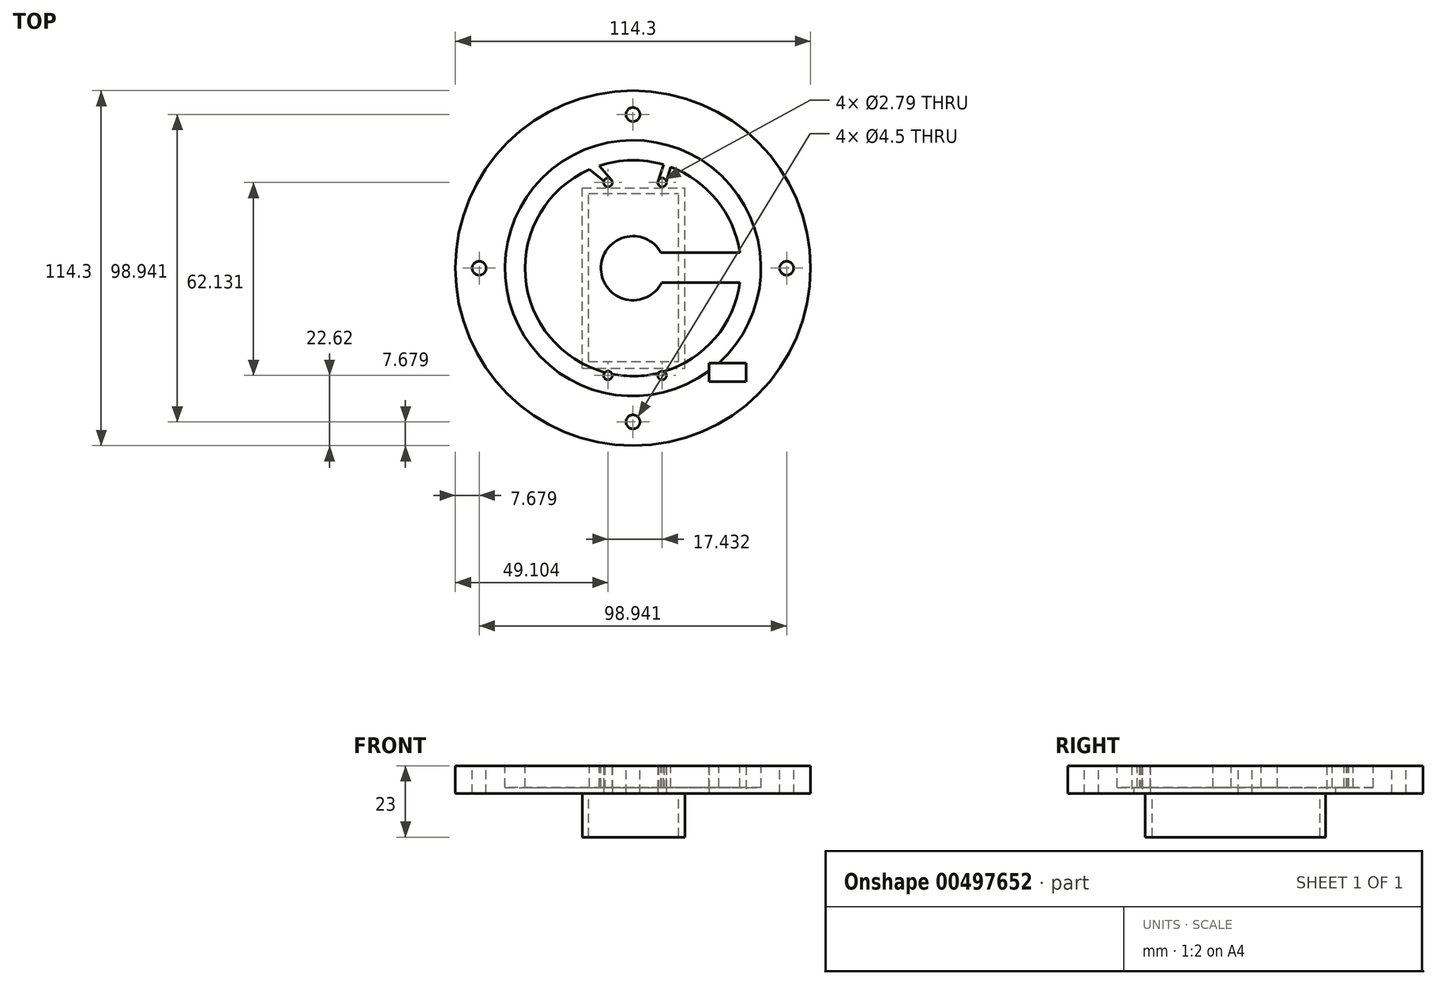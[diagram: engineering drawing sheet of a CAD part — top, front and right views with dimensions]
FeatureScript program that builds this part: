
annotation { "Feature Type Name" : "Feature", "Feature Type Description" : "" }
export const myFeature = defineFeature(function(context is Context, id is Id, definition is map)
    precondition{}
    {
        {
            var Q0;
            Q0=qCreatedBy(makeId("Top.planeOp"),FACE);
            var sketch = newSketch(context, id + "F0", { "sketchPlane" : qUnion([Q0])});
            skCircle(sketch, "E0", {"center": v(0, 0) * mm, "radius": 57.15 * mm});
            skLineSegment(sketch, "E1", {"start": v(0, 0) * mm, "end": v(-90.89, 0) * mm, "construction": true});
            skLineSegment(sketch, "E2", {"start": v(0, 0) * mm, "end": v(91.48, 0) * mm, "construction": true});
            skSolve(sketch);
        }
        {
            var Q0;
            Q0=makeQuery(id+"F0.imprint","IMPRINT",FACE,{"disambiguationData":[TD([[makeQuery(id+"F0.imprint","IMPRINT",EDGE,{"derivedFrom":sQuery(id+"F0.wireOp",EDGE,"E0")}),1.0]])]});
            extrude(context, id + "F1", {"entities" : qUnion([Q0]), "depth" : 9 * mm});
        }
        {
            var Q0;
            Q0=makeQuery(id+"F1.opExtrude","CAP_FACE",FACE,{"disambiguationData":[OSD([sQuery(id+"F0.wireOp",EDGE,"E0")])],"isStart":false});
            var sketch = newSketch(context, id + "F2", { "sketchPlane" : qUnion([Q0])});
            skCircle(sketch, "E3", {"center": v(0, 0) * mm, "radius": 41.18 * mm});
            skCircle(sketch, "E4", {"center": v(0, 0) * mm, "radius": 34.74 * mm});
            skSolve(sketch);
        }
        {
            var Q0;
            Q0=makeQuery(id+"F2.imprint","IMPRINT",FACE,{"disambiguationData":[TD([[makeQuery(id+"F2.imprint","IMPRINT",EDGE,{"derivedFrom":sQuery(id+"F2.wireOp",EDGE,"E3")}),1.0]])]});
            extrude(context, id + "F3", {"entities" : qUnion([Q0]), "operationType" : NewBodyOperationType.REMOVE, "oppositeDirection" : true, "depth" : 7 * mm});
        }
        {
            var Q0;
            Q0=makeQuery(id+"F3.boolean.opBoolean","SPLIT",FACE,{"disambiguationData":[TD([makeQuery(id+"F3.opExtrude","SWEPT_FACE",FACE,{"disambiguationData":[OSD([sQuery(id+"F2.wireOp",EDGE,"E4")])]})])],"derivedFrom":makeQuery(id+"F1.opExtrude","CAP_FACE",FACE,{"disambiguationData":[OSD([sQuery(id+"F0.wireOp",EDGE,"E0")])],"isStart":false})});
            var sketch = newSketch(context, id + "F4", { "sketchPlane" : qUnion([Q0])});
            skCircle(sketch, "E5", {"center": v(0, 0) * mm, "radius": 10.31 * mm});
            skLineSegment(sketch, "E6.bottom", {"start": v(8.97, 5.07) * mm, "end": v(37.77, 5.07) * mm});
            skLineSegment(sketch, "E6.top", {"start": v(8.97, -4.58) * mm, "end": v(37.77, -4.58) * mm});
            skLineSegment(sketch, "E6.left", {"start": v(8.97, 5.07) * mm, "end": v(8.97, -4.58) * mm});
            skLineSegment(sketch, "E6.right", {"start": v(37.77, 5.07) * mm, "end": v(37.77, -4.58) * mm});
            skSolve(sketch);
        }
        {
            var Q0;
            {var subQ0=sQuery(id+"F4.wireOp",EDGE,"E6.left");Q0=makeQuery(id+"F4.imprint","IMPRINT",FACE,{"disambiguationData":[TD([[makeQuery(id+"F4.imprint","IMPRINT",EDGE,{"derivedFrom":subQ0}),1.0]])]});}
            var Q1;
            {var subQ0=sQuery(id+"F4.wireOp",EDGE,"E6.right");Q1=makeQuery(id+"F4.imprint","IMPRINT",FACE,{"disambiguationData":[TD([[makeQuery(id+"F4.imprint","IMPRINT",EDGE,{"derivedFrom":subQ0}),-1.0]])]});}
            var Q2;
            {var subQ0=sQuery(id+"F4.wireOp",EDGE,"E6.left");Q2=makeQuery(id+"F4.imprint","IMPRINT",FACE,{"disambiguationData":[TD([[makeQuery(id+"F4.imprint","IMPRINT",EDGE,{"derivedFrom":subQ0}),-1.0]])]});}
            var Q3;
            {var subQ1=sQuery(id+"F4.wireOp",EDGE,"E5");var subQ3=sQuery(id+"F4.wireOp",EDGE,"E6.top");var subQ4=makeQuery(id+"F4.imprint","INTERSECT",VERTEX,{"derivedFrom":[subQ1,subQ3]});Q3=makeQuery(id+"F4.imprint","IMPRINT",FACE,{"disambiguationData":[TD([[makeQuery(id+"F4.imprint","IMPRINT",EDGE,{"disambiguationData":[TD([[subQ4,-1.0]])],"derivedFrom":subQ3}),1.0]])]});}
            extrude(context, id + "F5", {"entities" : qUnion([Q0, Q1, Q2, Q3]), "operationType" : NewBodyOperationType.REMOVE, "oppositeDirection" : true, "depth" : 7 * mm});
        }
        {
            var Q0;
            Q0=makeQuery(id+"F1.opExtrude","CAP_FACE",FACE,{"disambiguationData":[OSD([sQuery(id+"F0.wireOp",EDGE,"E0")])],"isStart":true});
            var sketch = newSketch(context, id + "F6", { "sketchPlane" : qUnion([Q0])});
            skLineSegment(sketch, "E7.bottom", {"start": v(24.43, 36.54) * mm, "end": v(36.43, 36.54) * mm});
            skLineSegment(sketch, "E7.top", {"start": v(24.43, 30.54) * mm, "end": v(36.43, 30.54) * mm});
            skLineSegment(sketch, "E7.left", {"start": v(24.43, 36.54) * mm, "end": v(24.43, 30.54) * mm});
            skLineSegment(sketch, "E7.right", {"start": v(36.43, 36.54) * mm, "end": v(36.43, 30.54) * mm});
            skSolve(sketch);
        }
        {
            var Q0;
            Q0=qSketchRegion(id+"F6",true);
            extrude(context, id + "F7", {"entities" : qUnion([Q0]), "operationType" : NewBodyOperationType.REMOVE, "oppositeDirection" : true, "depth" : 9 * mm});
        }
        {
            var Q0;
            {var subQ0=sQuery(id+"F0.wireOp",EDGE,"E0");Q0=makeQuery(id+"F3.boolean.opBoolean","SPLIT",FACE,{"disambiguationData":[TD([makeQuery(id+"F1.opExtrude","SWEPT_FACE",FACE,{"disambiguationData":[OSD([subQ0])]})])],"derivedFrom":makeQuery(id+"F1.opExtrude","CAP_FACE",FACE,{"disambiguationData":[OSD([subQ0])],"isStart":false})});}
            var sketch = newSketch(context, id + "F8", { "sketchPlane" : qUnion([Q0])});
            skCircle(sketch, "E8", {"center": v(0, 0) * mm, "radius": 49.47 * mm});
            skPoint(sketch, "E9", {"position": v(0, 49.47) * mm});
            skPoint(sketch, "E10", {"position": v(0, -49.47) * mm});
            skPoint(sketch, "E11", {"position": v(49.47, 0) * mm});
            skPoint(sketch, "E12", {"position": v(-49.47, 0) * mm});
            skSolve(sketch);
        }
        {
            var Q0;
            Q0=sQuery(id+"F8.wireOp",VERTEX,"E9");
            var Q1;
            Q1=sQuery(id+"F8.wireOp",VERTEX,"E12");
            var Q2;
            Q2=sQuery(id+"F8.wireOp",VERTEX,"E10");
            var Q3;
            Q3=sQuery(id+"F8.wireOp",VERTEX,"E11");
            var Q4;
            Q4=makeQuery(id+"F1.opExtrude","SWEPT_BODY",BODY,{"disambiguationData":[OSD([sQuery(id+"F0.wireOp",EDGE,"E0")])]});
            hole(context, id + "F9", {"style" : HoleStyle.SIMPLE, "endStyle" : HoleEndStyle.THROUGH, "standardTappedOrClearance" : lookupTablePath({ "standard" : "ANSI", "fit" : "Normal (ASME)", "size" : "#8", "type" : "Clearance" }), "standardBlindInLast" : lookupTablePath({ "fit" : "Free", "standard" : "ANSI", "size" : "#8", "type" : "Clearance" }), "holeDiameter" : 4.5 * mm, "isTappedThrough" : true, "tappedDepth" : 12.7 * mm, "tapClearance" : 3, "locations" : qUnion([Q0, Q1, Q2, Q3]), "scope" : qUnion([Q4])});
        }
        {
            var Q0;
            Q0=makeQuery(id+"F1.opExtrude","CAP_FACE",FACE,{"disambiguationData":[OSD([sQuery(id+"F0.wireOp",EDGE,"E0")])],"isStart":true});
            var sketch = newSketch(context, id + "F10", { "sketchPlane" : qUnion([Q0])});
            skLineSegment(sketch, "E13.bottom", {"start": v(-14.3, 29.98) * mm, "end": v(14.7, 29.98) * mm});
            skLineSegment(sketch, "E13.top", {"start": v(-14.3, -24.02) * mm, "end": v(14.7, -24.02) * mm});
            skLineSegment(sketch, "E13.left", {"start": v(-14.3, 29.98) * mm, "end": v(-14.3, -24.02) * mm});
            skLineSegment(sketch, "E13.right", {"start": v(14.7, 29.98) * mm, "end": v(14.7, -24.02) * mm});
            skLineSegment(sketch, "E14.bottom", {"start": v(-16.31, 32.19) * mm, "end": v(16.69, 32.19) * mm});
            skLineSegment(sketch, "E14.top", {"start": v(-16.31, -25.81) * mm, "end": v(16.69, -25.81) * mm});
            skLineSegment(sketch, "E14.left", {"start": v(-16.31, 32.19) * mm, "end": v(-16.31, -25.81) * mm});
            skLineSegment(sketch, "E14.right", {"start": v(16.69, 32.19) * mm, "end": v(16.69, -25.81) * mm});
            skSolve(sketch);
        }
        {
            var Q0;
            Q0=makeQuery(id+"F10.imprint","IMPRINT",FACE,{"disambiguationData":[TD([[makeQuery(id+"F10.imprint","IMPRINT",EDGE,{"derivedFrom":sQuery(id+"F10.wireOp",EDGE,"E13.bottom")}),1.0]])]});
            extrude(context, id + "F11", {"entities" : qUnion([Q0]), "operationType" : NewBodyOperationType.ADD, "depth" : 14 * mm});
        }
        {
            var Q0;
            {var subQ0=sQuery(id+"F0.wireOp",EDGE,"E0");Q0=makeQuery(id+"F11.boolean.opBoolean","SPLIT",FACE,{"disambiguationData":[TD([makeQuery(id+"F1.opExtrude","SWEPT_FACE",FACE,{"disambiguationData":[OSD([subQ0])]})])],"derivedFrom":makeQuery(id+"F1.opExtrude","CAP_FACE",FACE,{"disambiguationData":[OSD([subQ0])],"isStart":true})});}
            var sketch = newSketch(context, id + "F12", { "sketchPlane" : qUnion([Q0])});
            skPoint(sketch, "E15", {"position": v(-8.05, 34.53) * mm});
            skPoint(sketch, "E16", {"position": v(9.39, 34.53) * mm});
            skPoint(sketch, "E17", {"position": v(-8.05, -27.6) * mm});
            skPoint(sketch, "E18", {"position": v(9.39, -27.6) * mm});
            skSolve(sketch);
        }
        {
            var Q0;
            Q0=sQuery(id+"F12.wireOp",VERTEX,"E15");
            var Q1;
            Q1=sQuery(id+"F12.wireOp",VERTEX,"E16");
            var Q2;
            Q2=sQuery(id+"F12.wireOp",VERTEX,"E17");
            var Q3;
            Q3=sQuery(id+"F12.wireOp",VERTEX,"E18");
            var Q4;
            Q4=makeQuery(id+"F1.opExtrude","SWEPT_BODY",BODY,{"disambiguationData":[OSD([sQuery(id+"F0.wireOp",EDGE,"E0")])]});
            hole(context, id + "F13", {"style" : HoleStyle.SIMPLE, "endStyle" : HoleEndStyle.THROUGH, "standardTappedOrClearance" : lookupTablePath({ "standard" : "ANSI", "fit" : "Normal (ASME)", "size" : "#3", "type" : "Clearance" }), "standardBlindInLast" : lookupTablePath({ "fit" : "Free", "standard" : "ANSI", "size" : "#3", "type" : "Clearance" }), "holeDiameter" : 2.8 * mm, "isTappedThrough" : true, "tappedDepth" : 12.7 * mm, "tapClearance" : 3, "locations" : qUnion([Q0, Q1, Q2, Q3]), "scope" : qUnion([Q4])});
        }
        {
            var Q0;
            Q0=makeQuery(id+"F3.boolean.opBoolean","SPLIT",FACE,{"disambiguationData":[TD([makeQuery(id+"F3.opExtrude","SWEPT_FACE",FACE,{"disambiguationData":[OSD([sQuery(id+"F2.wireOp",EDGE,"E4")])]})])],"derivedFrom":makeQuery(id+"F1.opExtrude","CAP_FACE",FACE,{"disambiguationData":[OSD([sQuery(id+"F0.wireOp",EDGE,"E0")])],"isStart":false})});
            var sketch = newSketch(context, id + "F14", { "sketchPlane" : qUnion([Q0])});
            skLineSegment(sketch, "E19", {"start": v(-9.37, 28.04) * mm, "end": v(-14.06, 31.76) * mm});
            skLineSegment(sketch, "E20", {"start": v(-11.71, 34.07) * mm, "end": v(-6.98, 28.5) * mm});
            skPoint(sketch, "E20.startSnap0", {"position": v(-11.71, 29.9) * mm});
            skLineSegment(sketch, "E21", {"start": v(8.06, 28.04) * mm, "end": v(10.23, 34.63) * mm});
            skLineSegment(sketch, "E22", {"start": v(10.71, 28.04) * mm, "end": v(12.53, 33.75) * mm});
            skSolve(sketch);
        }
        {
            var Q0;
            {var subQ0=sQuery(id+"F14.wireOp",EDGE,"E19");Q0=makeQuery(id+"F14.imprint","IMPRINT",FACE,{"disambiguationData":[TD([[makeQuery(id+"F14.imprint","IMPRINT",EDGE,{"derivedFrom":subQ0}),-1.0]])]});}
            var Q1;
            {var subQ0=sQuery(id+"F14.wireOp",EDGE,"E21");var subQ1=sQuery(id+"F2.wireOp",EDGE,"E4");var subQ2=makeQuery(id+"F3.opExtrude","SWEPT_FACE",FACE,{"disambiguationData":[OSD([subQ1])]});var subQ3=makeQuery(id+"F1.opExtrude","CAP_FACE",FACE,{"disambiguationData":[OSD([sQuery(id+"F0.wireOp",EDGE,"E0")])],"isStart":false});var subQ4=makeQuery(id+"F13.hole-3.boolean.opBoolean","INTERSECT",EDGE,{"derivedFrom":[makeQuery(id+"F3.boolean.opBoolean","SPLIT",FACE,{"disambiguationData":[TD([subQ2])],"derivedFrom":subQ3}),makeQuery(id+"F13.hole-3.opRevolve","SWEPT_FACE",FACE,{"disambiguationData":[OSD([sQuery(id+"F13.hole-3.sketch.wireOp",EDGE,"core_line_2")])]})]});var subQ5=makeQuery(id+"F14.imprint","INTERSECT",VERTEX,{"derivedFrom":[subQ4,subQ0]});Q1=makeQuery(id+"F14.imprint","IMPRINT",FACE,{"disambiguationData":[TD([[makeQuery(id+"F14.imprint","IMPRINT",EDGE,{"disambiguationData":[TD([[subQ5,-1.0]])],"derivedFrom":subQ0}),-1.0]])]});}
            extrude(context, id + "F15", {"entities" : qUnion([Q0, Q1]), "operationType" : NewBodyOperationType.REMOVE, "oppositeDirection" : true, "depth" : 7 * mm});
        }
    });
